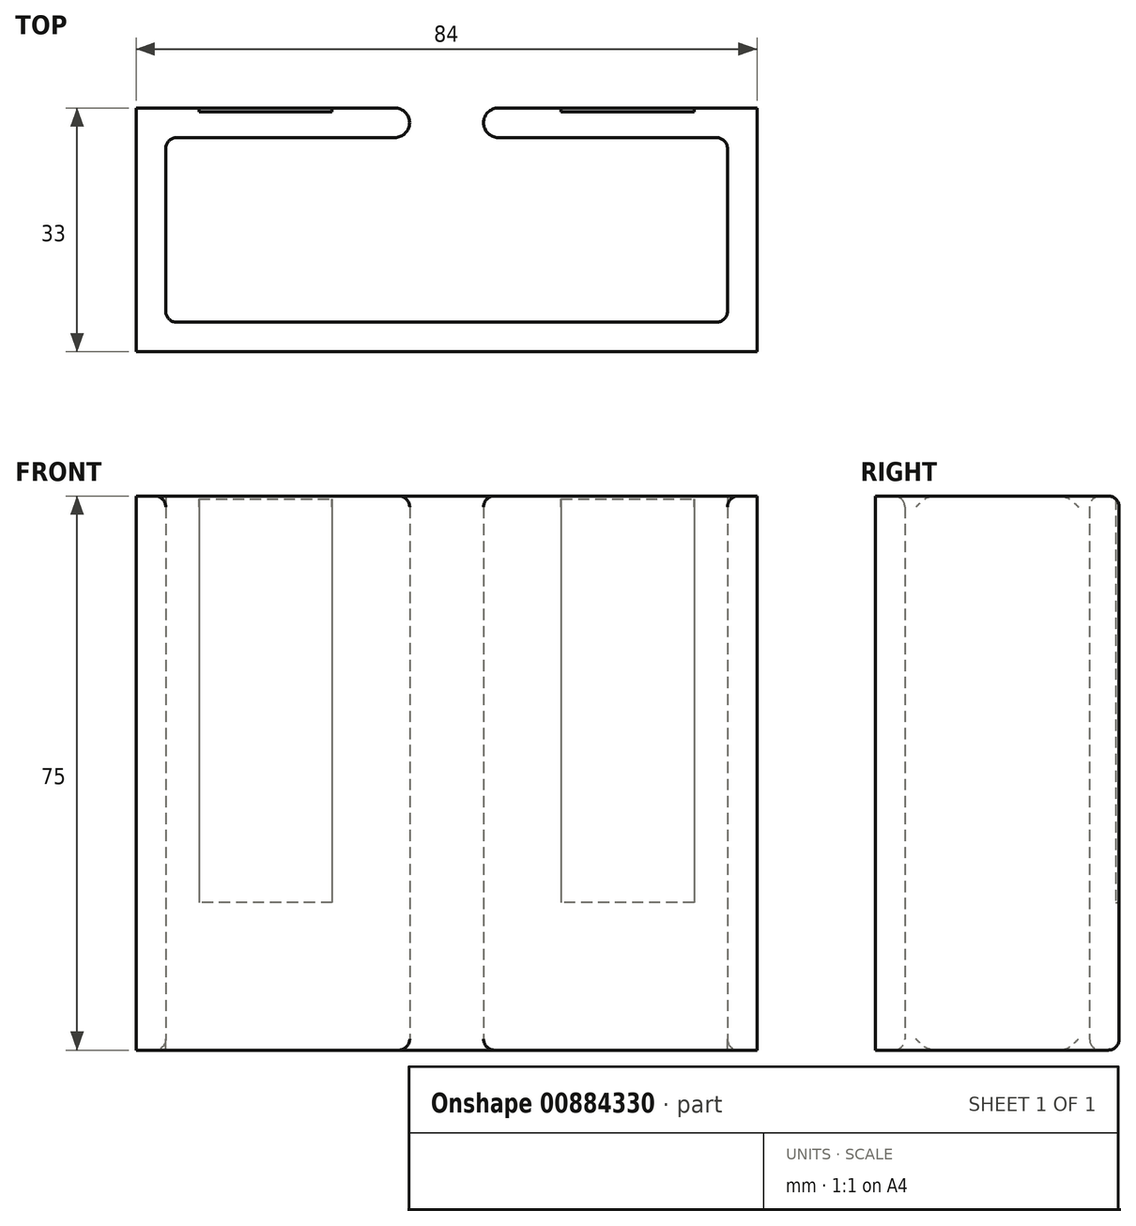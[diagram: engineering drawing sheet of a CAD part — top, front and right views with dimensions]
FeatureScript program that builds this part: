
annotation { "Feature Type Name" : "Feature", "Feature Type Description" : "" }
export const myFeature = defineFeature(function(context is Context, id is Id, definition is map)
    precondition{}
    {
        {
            var Q0;
            Q0=qCreatedBy(makeId("Top.planeOp"),FACE);
            var sketch = newSketch(context, id + "F0", { "sketchPlane" : qUnion([Q0])});
            skLineSegment(sketch, "E0.bottom", {"start": v(38, -12.5) * mm, "end": v(-38, -12.5) * mm});
            skLineSegment(sketch, "E0.top", {"start": v(38, 12.5) * mm, "end": v(7, 12.5) * mm});
            skLineSegment(sketch, "E0.left", {"start": v(38, -12.5) * mm, "end": v(38, 12.5) * mm});
            skLineSegment(sketch, "E0.right", {"start": v(-38, -12.5) * mm, "end": v(-38, 12.5) * mm});
            skPoint(sketch, "E0.middle", {"position": v(0, 0) * mm});
            skLineSegment(sketch, "E1.0", {"start": v(42, 16.5) * mm, "end": v(7, 16.5) * mm});
            skLineSegment(sketch, "E1.1", {"start": v(42, -16.5) * mm, "end": v(42, 16.5) * mm});
            skLineSegment(sketch, "E1.2", {"start": v(42, -16.5) * mm, "end": v(-42, -16.5) * mm});
            skLineSegment(sketch, "E1.3", {"start": v(-42, -16.5) * mm, "end": v(-42, 16.5) * mm});
            skLineSegment(sketch, "E2", {"start": v(0, 0) * mm, "end": v(0, 48.13) * mm, "construction": true});
            skLineSegment(sketch, "E3", {"start": v(0, 18.5) * mm, "end": v(-7, 18.5) * mm, "construction": true});
            skLineSegment(sketch, "E4.MirrorCS", {"start": v(0, 18.5) * mm, "end": v(7, 18.5) * mm, "construction": true});
            skArc(sketch, "E5", {"start": v(-7, 12.5) * mm, "mid": v(-5, 14.5) * mm, "end": v(-7, 16.5) * mm});
            skArc(sketch, "E6", {"start": v(7, 16.5) * mm, "mid": v(5, 14.5) * mm, "end": v(7, 12.5) * mm});
            skLineSegment(sketch, "E7.trimOffspring", {"start": v(-7, 16.5) * mm, "end": v(-42, 16.5) * mm});
            skLineSegment(sketch, "E8.trimOffspring", {"start": v(-7, 12.5) * mm, "end": v(-38, 12.5) * mm});
            skSolve(sketch);
        }
        {
            var Q0;
            Q0=makeQuery(id+"F0.imprint","IMPRINT",FACE,{"disambiguationData":[TD([[makeQuery(id+"F0.imprint","IMPRINT",EDGE,{"derivedFrom":sQuery(id+"F0.wireOp",EDGE,"E0.bottom")}),1.0]])]});
            var Q1;
            Q1 = qSketchRegion(id + "F4", true);
            extrude(context, id + "F1", {"entities" : qUnion([Q0, Q1]), "depth" : 75 * mm, "offsetDistance" : 25 * mm});
        }
        {
            var Q0;
            Q0=makeQuery(id+"F1.opExtrude","SWEPT_FACE",FACE,{"disambiguationData":[OSD([sQuery(id+"F0.wireOp",EDGE,"E0.bottom")])]});
            var Q1;
            Q1=makeQuery(id+"F1.opExtrude","SWEPT_FACE",FACE,{"disambiguationData":[OSD([sQuery(id+"F0.wireOp",EDGE,"E8.trimOffspring")])]});
            var Q2;
            Q2=makeQuery(id+"F1.opExtrude","SWEPT_FACE",FACE,{"disambiguationData":[OSD([sQuery(id+"F0.wireOp",EDGE,"E0.top")])]});
            fillet(context, id + "F2", {"entities" : qUnion([Q0, Q1, Q2]), "radius" : 1.5 * mm, "tangentPropagation" : true, "allowEdgeOverflow" : false});
        }
        {
            var Q0;
            Q0=makeQuery(id+"F1.opExtrude","SWEPT_FACE",FACE,{"disambiguationData":[OSD([sQuery(id+"F0.wireOp",EDGE,"E1.0")])]});
            cPlane(context, id + "F3", {"entities" : qUnion([Q0]), "cplaneType" : CPlaneType.OFFSET, "offset" : 0 * mm, "width" : 150 * mm, "height" : 150 * mm});
        }
        {
            var Q0;
            Q0=qCreatedBy(id+"F3.planeOp",FACE);
            var sketch = newSketch(context, id + "F4", { "sketchPlane" : qUnion([Q0])});
            skLineSegment(sketch, "E9.0.0", {"start": v(-42, 73.5) * mm, "end": v(-42, 1.5) * mm, "construction": true});
            skLineSegment(sketch, "E9.0.1", {"start": v(-42, 1.5) * mm, "end": v(-7, 1.5) * mm, "construction": true});
            skLineSegment(sketch, "E9.0.2", {"start": v(-7, 1.5) * mm, "end": v(-7, 73.5) * mm, "construction": true});
            skLineSegment(sketch, "E9.0.3", {"start": v(-7, 73.5) * mm, "end": v(-42, 73.5) * mm, "construction": true});
            skLineSegment(sketch, "E9.1.0", {"start": v(7, 73.5) * mm, "end": v(7, 1.5) * mm, "construction": true});
            skLineSegment(sketch, "E9.1.1", {"start": v(7, 1.5) * mm, "end": v(42, 1.5) * mm, "construction": true});
            skLineSegment(sketch, "E9.1.2", {"start": v(42, 1.5) * mm, "end": v(42, 73.5) * mm, "construction": true});
            skLineSegment(sketch, "E10", {"start": v(24.5, 75) * mm, "end": v(24.5, 20) * mm, "construction": true});
            skLineSegment(sketch, "E11.0", {"start": v(15.5, 75) * mm, "end": v(15.5, 20) * mm});
            skLineSegment(sketch, "E12.MirrorCS", {"start": v(33.5, 75) * mm, "end": v(33.5, 20) * mm});
            skLineSegment(sketch, "E13.MirrorCS", {"start": v(-15.5, 75) * mm, "end": v(-15.5, 20) * mm});
            skLineSegment(sketch, "E14.MirrorCS", {"start": v(-33.5, 75) * mm, "end": v(-33.5, 20) * mm});
            skLineSegment(sketch, "E15", {"start": v(-33.5, 75) * mm, "end": v(-15.5, 75) * mm});
            skLineSegment(sketch, "E16", {"start": v(-33.5, 20) * mm, "end": v(-15.5, 20) * mm});
            skLineSegment(sketch, "E17", {"start": v(15.5, 20) * mm, "end": v(33.5, 20) * mm});
            skLineSegment(sketch, "E18", {"start": v(33.5, 75) * mm, "end": v(15.5, 75) * mm});
            skLineSegment(sketch, "E19.1", {"start": v(7, 75) * mm, "end": v(42, 75) * mm, "construction": true});
            skSolve(sketch);
        }
        {
            var Q0;
            Q0=makeQuery(id+"F4.imprint","IMPRINT",FACE,{"disambiguationData":[TD([[makeQuery(id+"F4.imprint","IMPRINT",EDGE,{"derivedFrom":sQuery(id+"F4.wireOp",EDGE,"E13.MirrorCS")}),-1.0]])]});
            var Q1;
            Q1=makeQuery(id+"F4.imprint","IMPRINT",FACE,{"disambiguationData":[TD([[makeQuery(id+"F4.imprint","IMPRINT",EDGE,{"derivedFrom":sQuery(id+"F4.wireOp",EDGE,"E11.0")}),1.0]])]});
            extrude(context, id + "F5", {"entities" : qUnion([Q0, Q1]), "operationType" : NewBodyOperationType.REMOVE, "oppositeDirection" : true, "depth" : .5 * mm, "offsetDistance" : 25 * mm});
        }
    });
